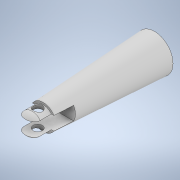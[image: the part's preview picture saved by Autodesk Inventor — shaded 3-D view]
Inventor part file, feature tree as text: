
AUTODESK INVENTOR PART (.ipt)
format: ipt  version: 2021 (Build 250183000, 183)  size: 141,312 bytes
history: native  units: mm
features: extrude x4, sketch x4, fillet x1
ambient origin geometry x8: Origin, YZ Plane, XZ Plane, XY Plane, X Axis, Y Axis, Z Axis, Center Point
bodies: Solid1 (feature_tree)
feature tree (9):
  extrude  "Extrusion1"  Depth=10.0mm
  extrude  "Extrusion2"  Depth=2.0mm
  fillet  "Fillet1"  Radius=2.5mm
  extrude  "Extrusion4"  Depth=10.0mm TaperAngle=0.0deg
  extrude  "Extrusion5"  [1 undecoded]
  sketch  "Sketch1"  dims[d0=10.0mm d1=30.0mm d2=-0.523599mm]
  sketch  "Sketch2"  dims[d3=5.0mm d4=0.0mm d5=2.0mm d8=2.5mm]
  sketch  "Sketch4"  dims[d9=10.0mm d10=0.0mm d11=10.0mm d12=0.0mm]
  sketch  "Sketch5"
note: 1 required parameter value undecoded (feature->parameter linkage not recoverable at this tier; creation-order binding heuristic only, values carry confidence <= 0.55)
